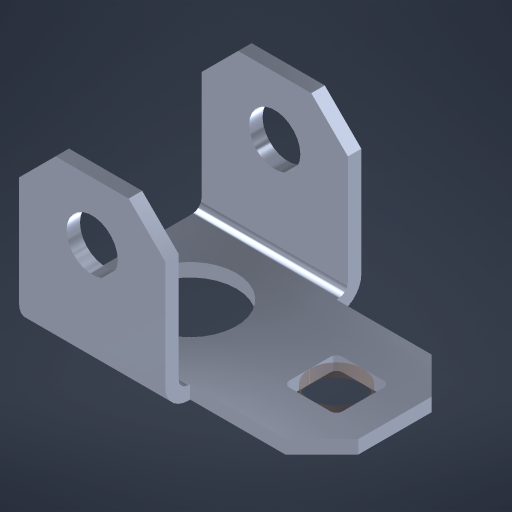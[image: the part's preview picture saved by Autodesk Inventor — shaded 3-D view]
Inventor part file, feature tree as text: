
AUTODESK INVENTOR PART (.ipt)
format: ipt  version: 2024 (Build 280153000, 153)  size: 307,712 bytes
history: native  units: in
note: dims shown in document units (in); Inventor stores cm internally (conversion verified against a paired STEP export)
features: other x3, sketch x2, delete_face x2, extrude x2, chamfer x1, split x1, imported_body x1
ambient origin geometry x8: Origin, YZ Plane, XZ Plane, XY Plane, X Axis, Y Axis, Z Axis, Center Point
bodies: Body1 (feature_tree), Body2 (feature_tree), Body3 (feature_tree)
feature tree (12):
  chamfer  "Chamfer1"  Distance=1.0in
  other  "VL-PNEU-PVT-0011"
  sketch  "Sketch1"  dims[d2=1.0in d3=0.0in]
  split  "Split1"
  delete_face  "Delete Face1"
  delete_face  "Delete Face2"
  imported_body  "Base1"
  other  "Srf1"
  other  "Srf2"
  sketch  "Sketch2"
  extrude  "ExtrusionSrf1"  [1 undecoded]
  extrude  "ExtrusionSrf2"  [1 undecoded]
note: 2 required parameter values undecoded (feature->parameter linkage not recoverable at this tier; creation-order binding heuristic only, values carry confidence <= 0.55)
